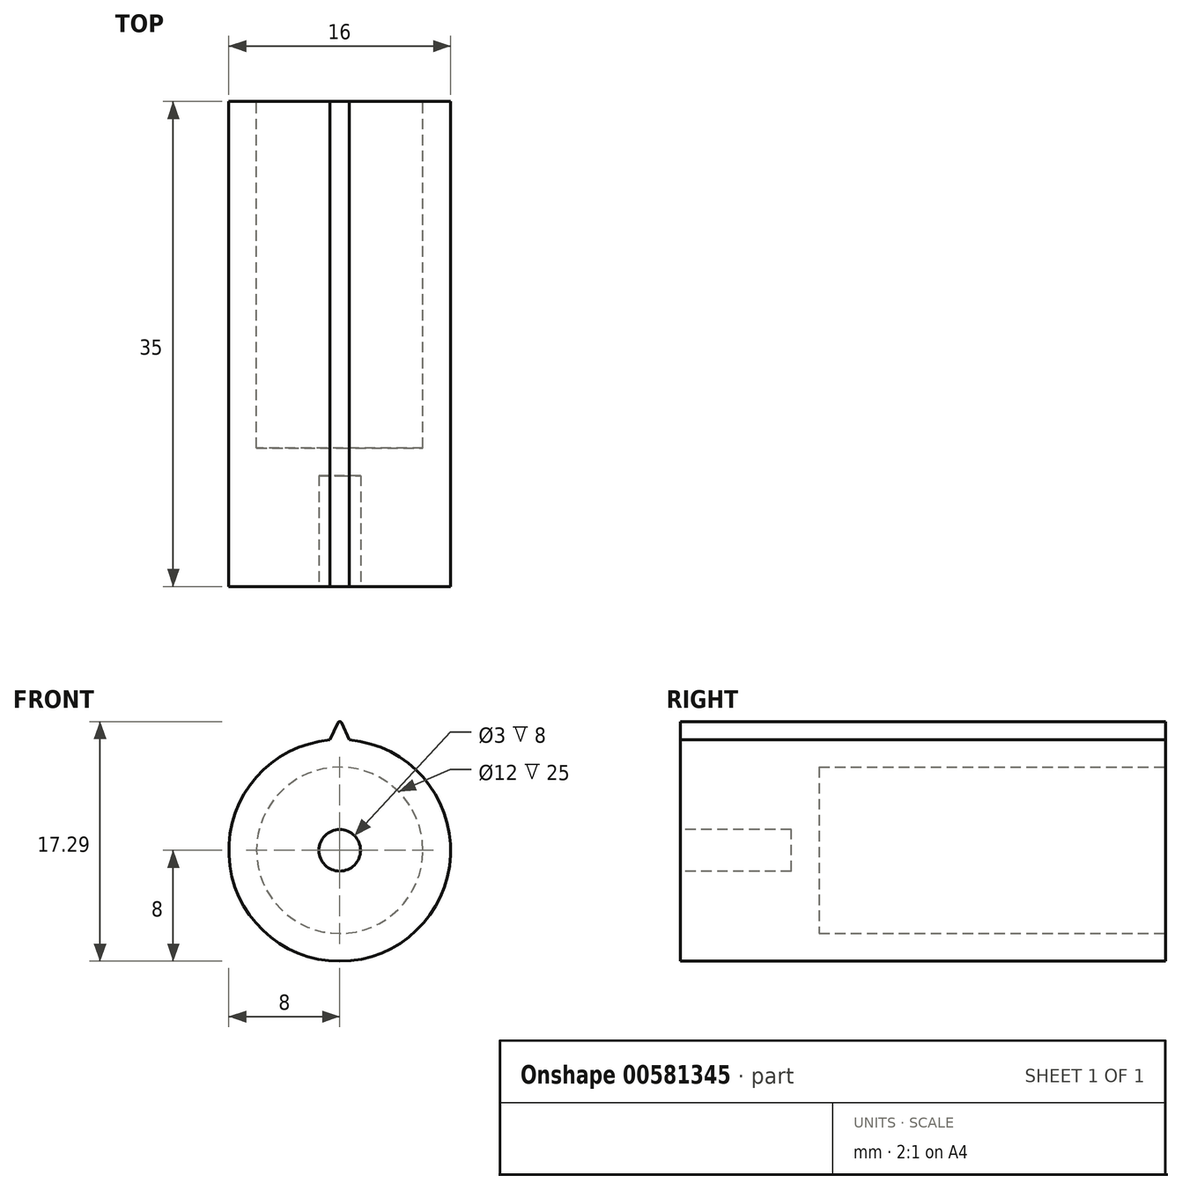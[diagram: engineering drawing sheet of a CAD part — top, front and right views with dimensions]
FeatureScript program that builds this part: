
annotation { "Feature Type Name" : "Feature", "Feature Type Description" : "" }
export const myFeature = defineFeature(function(context is Context, id is Id, definition is map)
    precondition{}
    {
        {
            var Q0;
            Q0=qCreatedBy(makeId("Front.planeOp"),FACE);
            var sketch = newSketch(context, id + "F0", { "sketchPlane" : qUnion([Q0])});
            skCircle(sketch, "E0", {"center": v(0, 0) * mm, "radius": 8 * mm});
            skCircle(sketch, "E1", {"center": v(0, 0) * mm, "radius": 5 * mm});
            skSolve(sketch);
        }
        {
            var Q0;
            Q0=makeQuery(id+"F0.imprint","IMPRINT",FACE,{"disambiguationData":[TD([[makeQuery(id+"F0.imprint","IMPRINT",EDGE,{"derivedFrom":sQuery(id+"F0.wireOp",EDGE,"E0")}),1.0]])]});
            var Q1;
            Q1=makeQuery(id+"F0.imprint","IMPRINT",FACE,{"disambiguationData":[TD([[makeQuery(id+"F0.imprint","IMPRINT",EDGE,{"derivedFrom":sQuery(id+"F0.wireOp",EDGE,"E1")}),1.0]])]});
            extrude(context, id + "F1", {"entities" : qUnion([Q0, Q1]), "depth" : 35 * mm, "offsetDistance" : 25 * mm});
        }
        {
            var Q0;
            Q0=makeQuery(id+"F0.imprint","IMPRINT",FACE,{"disambiguationData":[TD([[makeQuery(id+"F0.imprint","IMPRINT",EDGE,{"derivedFrom":sQuery(id+"F0.wireOp",EDGE,"E1")}),1.0]])]});
            extrude(context, id + "F2", {"entities" : qUnion([Q0]), "operationType" : NewBodyOperationType.ADD, "depth" : 20 * mm, "offsetDistance" : 25 * mm});
        }
        {
            var Q0;
            Q0=makeQuery(id+"F1.opExtrude","CAP_FACE",FACE,{"disambiguationData":[OSD([sQuery(id+"F0.wireOp",EDGE,"E0")])],"isStart":true});
            var sketch = newSketch(context, id + "F3", { "sketchPlane" : qUnion([Q0])});
            skSolve(sketch);
        }
        {
            var Q0;
            Q0=makeQuery(id+"F1.opExtrude","CAP_FACE",FACE,{"disambiguationData":[OSD([sQuery(id+"F0.wireOp",EDGE,"E0")])],"isStart":true});
            var sketch = newSketch(context, id + "F4", { "sketchPlane" : qUnion([Q0])});
            skLineSegment(sketch, "E2", {"start": v(0, 8) * mm, "end": v(0, 9.5) * mm, "construction": true});
            skLineSegment(sketch, "E3", {"start": v(0, 8) * mm, "end": v(-0.7, 7.97) * mm});
            skLineSegment(sketch, "E4", {"start": v(-0.7, 7.97) * mm, "end": v(0, 9.5) * mm});
            skLineSegment(sketch, "E5", {"start": v(0, 8) * mm, "end": v(0.7, 7.97) * mm});
            skLineSegment(sketch, "E6", {"start": v(0.7, 7.97) * mm, "end": v(0, 9.5) * mm});
            skSolve(sketch);
        }
        {
            var Q0;
            {var subQ0=sQuery(id+"F4.wireOp",EDGE,"E4");Q0=makeQuery(id+"F4.imprint","IMPRINT",FACE,{"disambiguationData":[TD([[makeQuery(id+"F4.imprint","IMPRINT",EDGE,{"derivedFrom":subQ0}),-1.0]])]});}
            extrude(context, id + "F5", {"entities" : qUnion([Q0]), "operationType" : NewBodyOperationType.ADD, "oppositeDirection" : true, "depth" : 35 * mm, "offsetDistance" : 25 * mm});
        }
        {
            var Q0;
            Q0=makeQuery(id+"F5.opExtrude","SWEPT_EDGE",EDGE,{"disambiguationData":[OSD([sQuery(id+"F0.wireOp",EDGE,"E0"),sQuery(id+"F4.wireOp",EDGE,"E3"),sQuery(id+"F4.wireOp",EDGE,"E4")])]});
            var Q1;
            Q1=makeQuery(id+"F5.opExtrude","SWEPT_EDGE",EDGE,{"disambiguationData":[OSD([sQuery(id+"F0.wireOp",EDGE,"E0"),sQuery(id+"F4.wireOp",EDGE,"E5"),sQuery(id+"F4.wireOp",EDGE,"E6")])]});
            var Q2;
            Q2=makeQuery(id+"F5.opExtrude","SWEPT_EDGE",EDGE,{"disambiguationData":[OSD([sQuery(id+"F4.wireOp",EDGE,"E4"),sQuery(id+"F4.wireOp",EDGE,"E6")])]});
            fillet(context, id + "F6", {"entities" : qUnion([Q0, Q1, Q2]), "radius" : .15 * mm, "tangentPropagation" : true, "allowEdgeOverflow" : false});
        }
        {
            var Q0;
            Q0=makeQuery(id+"F1.opExtrude","CAP_FACE",FACE,{"disambiguationData":[OSD([sQuery(id+"F0.wireOp",EDGE,"E0")])],"isStart":false});
            var sketch = newSketch(context, id + "F7", { "sketchPlane" : qUnion([Q0])});
            skCircle(sketch, "E7", {"center": v(0, 0) * mm, "radius": 1.5 * mm});
            skSolve(sketch);
        }
        {
            var Q0;
            Q0=makeQuery(id+"F7.imprint","IMPRINT",FACE,{"disambiguationData":[TD([[makeQuery(id+"F7.imprint","IMPRINT",EDGE,{"derivedFrom":sQuery(id+"F7.wireOp",EDGE,"E7")}),1.0]])]});
            extrude(context, id + "F8", {"entities" : qUnion([Q0]), "operationType" : NewBodyOperationType.REMOVE, "oppositeDirection" : true, "depth" : 8 * mm, "offsetDistance" : 25 * mm});
        }
        {
            var Q0;
            Q0=makeQuery(id+"F3.imprint","IMPRINT",FACE,{"disambiguationData":[TD([[makeQuery(id+"F3.imprint","IMPRINT",EDGE,{"derivedFrom":makeQuery(id+"F1.opExtrude","CAP_EDGE",EDGE,{"disambiguationData":[OSD([sQuery(id+"F0.wireOp",EDGE,"E0")])],"isStart":true})}),-1.0]])]});
            var sketch = newSketch(context, id + "F9", { "sketchPlane" : qUnion([Q0])});
            skCircle(sketch, "E8", {"center": v(0, 0) * mm, "radius": 6 * mm});
            skSolve(sketch);
        }
        {
            var Q0;
            Q0=makeQuery(id+"F9.imprint","IMPRINT",FACE,{"disambiguationData":[TD([[makeQuery(id+"F9.imprint","IMPRINT",EDGE,{"derivedFrom":sQuery(id+"F9.wireOp",EDGE,"E8")}),1.0]])]});
            var Q1;
            Q1=sQuery(id+"F9.wireOp",EDGE,"E8");
            extrude(context, id + "F10", {"entities" : qUnion([Q0]), "operationType" : NewBodyOperationType.REMOVE, "surfaceEntities" : qUnion([Q1]), "oppositeDirection" : true, "depth" : 25 * mm, "offsetDistance" : 25 * mm});
        }
    });
